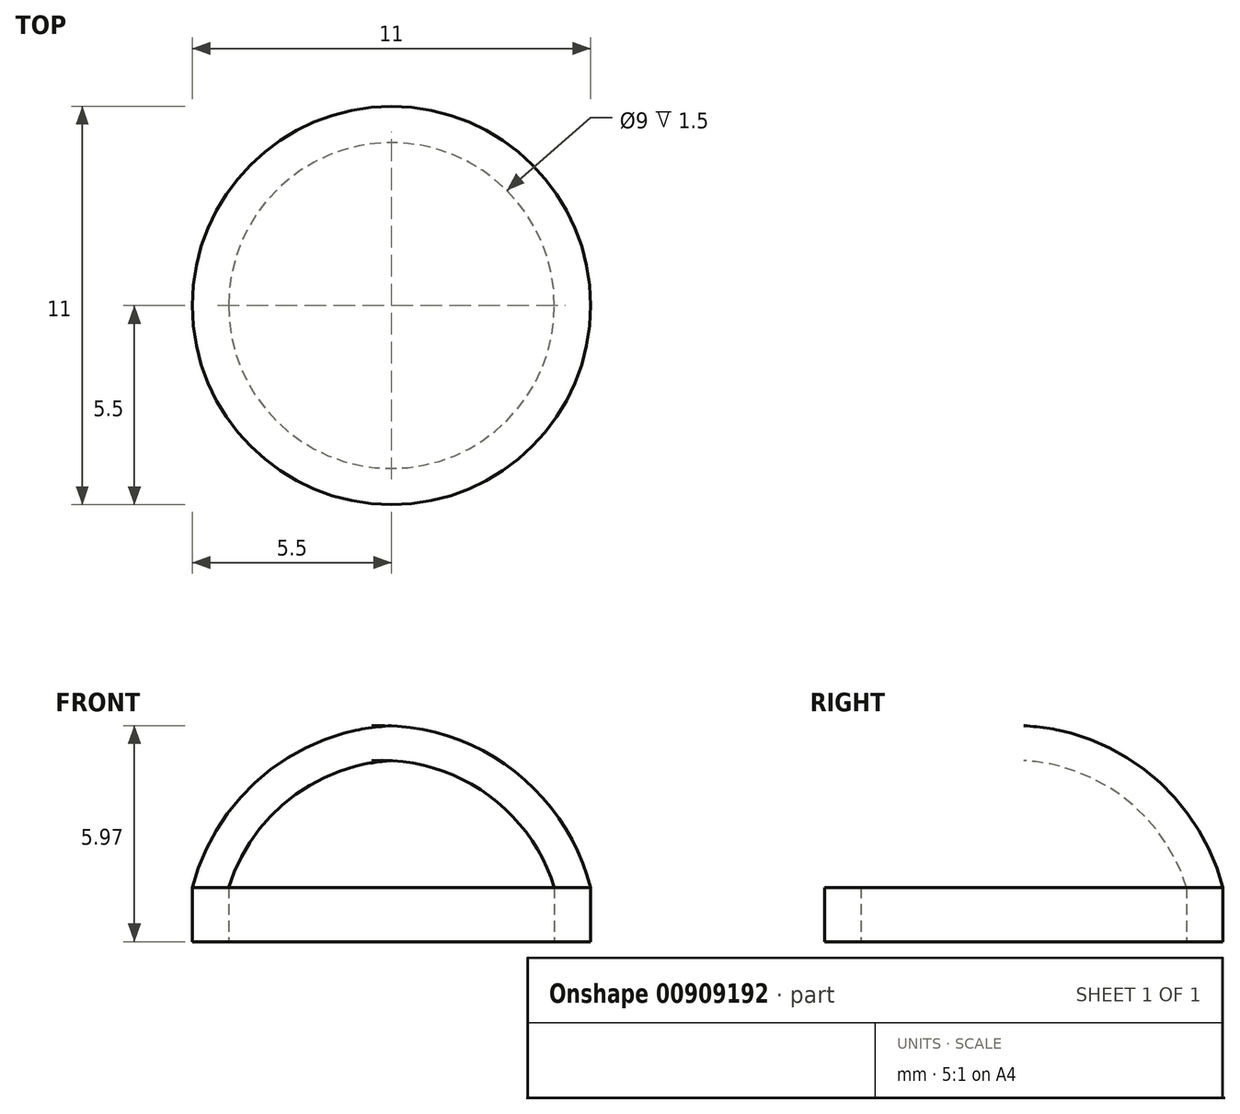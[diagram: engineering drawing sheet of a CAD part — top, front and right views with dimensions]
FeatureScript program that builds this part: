
annotation { "Feature Type Name" : "Feature", "Feature Type Description" : "" }
export const myFeature = defineFeature(function(context is Context, id is Id, definition is map)
    precondition{}
    {
        {
            var Q0;
            Q0=qCreatedBy(makeId("Top.planeOp"),FACE);
            var sketch = newSketch(context, id + "F0", { "sketchPlane" : qUnion([Q0])});
            skCircle(sketch, "E0", {"center": v(0, 0) * mm, "radius": 4.5 * mm});
            skCircle(sketch, "E1.0", {"center": v(0, 0) * mm, "radius": 5.5 * mm});
            skSolve(sketch);
        }
        {
            var Q0;
            Q0=makeQuery(id+"F0.imprint","IMPRINT",FACE,{"disambiguationData":[TD([[makeQuery(id+"F0.imprint","IMPRINT",EDGE,{"derivedFrom":sQuery(id+"F0.wireOp",EDGE,"E0")}),-1.0]])]});
            extrude(context, id + "F1", {"entities" : qUnion([Q0]), "depth" : 1.5 * mm, "offsetDistance" : 25 * mm});
        }
        {
            var Q0;
            Q0=qCreatedBy(makeId("Front.planeOp"),FACE);
            var sketch = newSketch(context, id + "F2", { "sketchPlane" : qUnion([Q0])});
            skLineSegment(sketch, "E2", {"start": v(0, 0) * mm, "end": v(0, 5) * mm, "construction": true});
            skLineSegment(sketch, "E3.0", {"start": v(-4.5, 1.5) * mm, "end": v(4.5, 1.5) * mm, "construction": true});
            skArc(sketch, "E4", {"start": v(4.5, 1.5) * mm, "mid": v(2.8, 3.95) * mm, "end": v(0, 5) * mm});
            skArc(sketch, "E5", {"start": v(5.5, 1.5) * mm, "mid": v(3.48, 4.64) * mm, "end": v(0, 5.96) * mm});
            skLineSegment(sketch, "E6.0", {"start": v(-5.5, 1.5) * mm, "end": v(5.5, 1.5) * mm, "construction": true});
            skLineSegment(sketch, "E7", {"start": v(0, 5.96) * mm, "end": v(0, 5) * mm});
            skLineSegment(sketch, "E8", {"start": v(4.5, 1.5) * mm, "end": v(5.5, 1.5) * mm});
            skSolve(sketch);
        }
        {
            var Q0;
            Q0=makeQuery(id+"F2.imprint","IMPRINT",FACE,{"disambiguationData":[TD([[makeQuery(id+"F2.imprint","IMPRINT",EDGE,{"derivedFrom":sQuery(id+"F2.wireOp",EDGE,"E4")}),-1.0]])]});
            var Q1;
            Q1=sQuery(id+"F2.wireOp",EDGE,"E2");
            revolve(context, id + "F3", {"operationType" : NewBodyOperationType.ADD, "surfaceOperationType" : NewSurfaceOperationType.NEW, "entities" : qUnion([Q0]), "axis" : qUnion([Q1]), "revolveType" : RevolveType.FULL});
        }
    });
